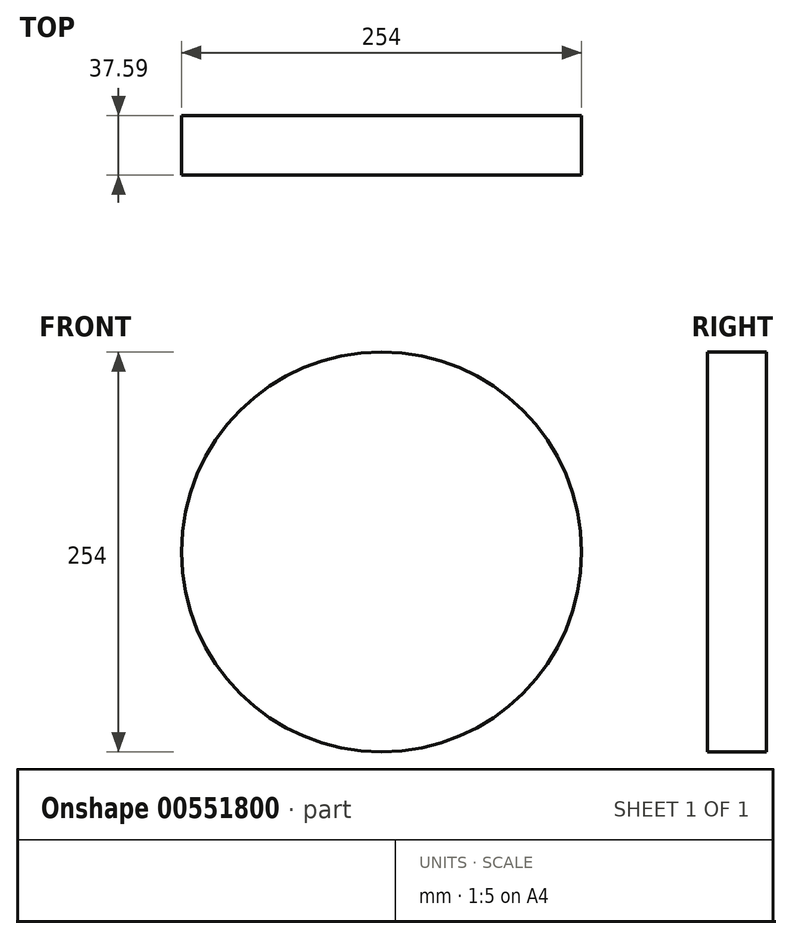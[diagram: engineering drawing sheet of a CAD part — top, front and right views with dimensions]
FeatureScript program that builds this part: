
annotation { "Feature Type Name" : "Feature", "Feature Type Description" : "" }
export const myFeature = defineFeature(function(context is Context, id is Id, definition is map)
    precondition{}
    {
        {
            var Q0;
            Q0=qCreatedBy(makeId("Front.planeOp"),FACE);
            var sketch = newSketch(context, id + "F0", { "sketchPlane" : qUnion([Q0])});
            skCircle(sketch, "E0", {"center": v(0, 0) * mm, "radius": 127 * mm});
            skSolve(sketch);
        }
        {
            var Q0;
            Q0=makeQuery(id+"F0.imprint","IMPRINT",FACE,{"disambiguationData":[TD([[makeQuery(id+"F0.imprint","IMPRINT",EDGE,{"derivedFrom":sQuery(id+"F0.wireOp",EDGE,"E0")}),1.0]])]});
            extrude(context, id + "F1", {"entities" : qUnion([Q0]), "depth" : 37.6 * mm, "offsetDistance" : 25.4 * mm});
        }
    });
